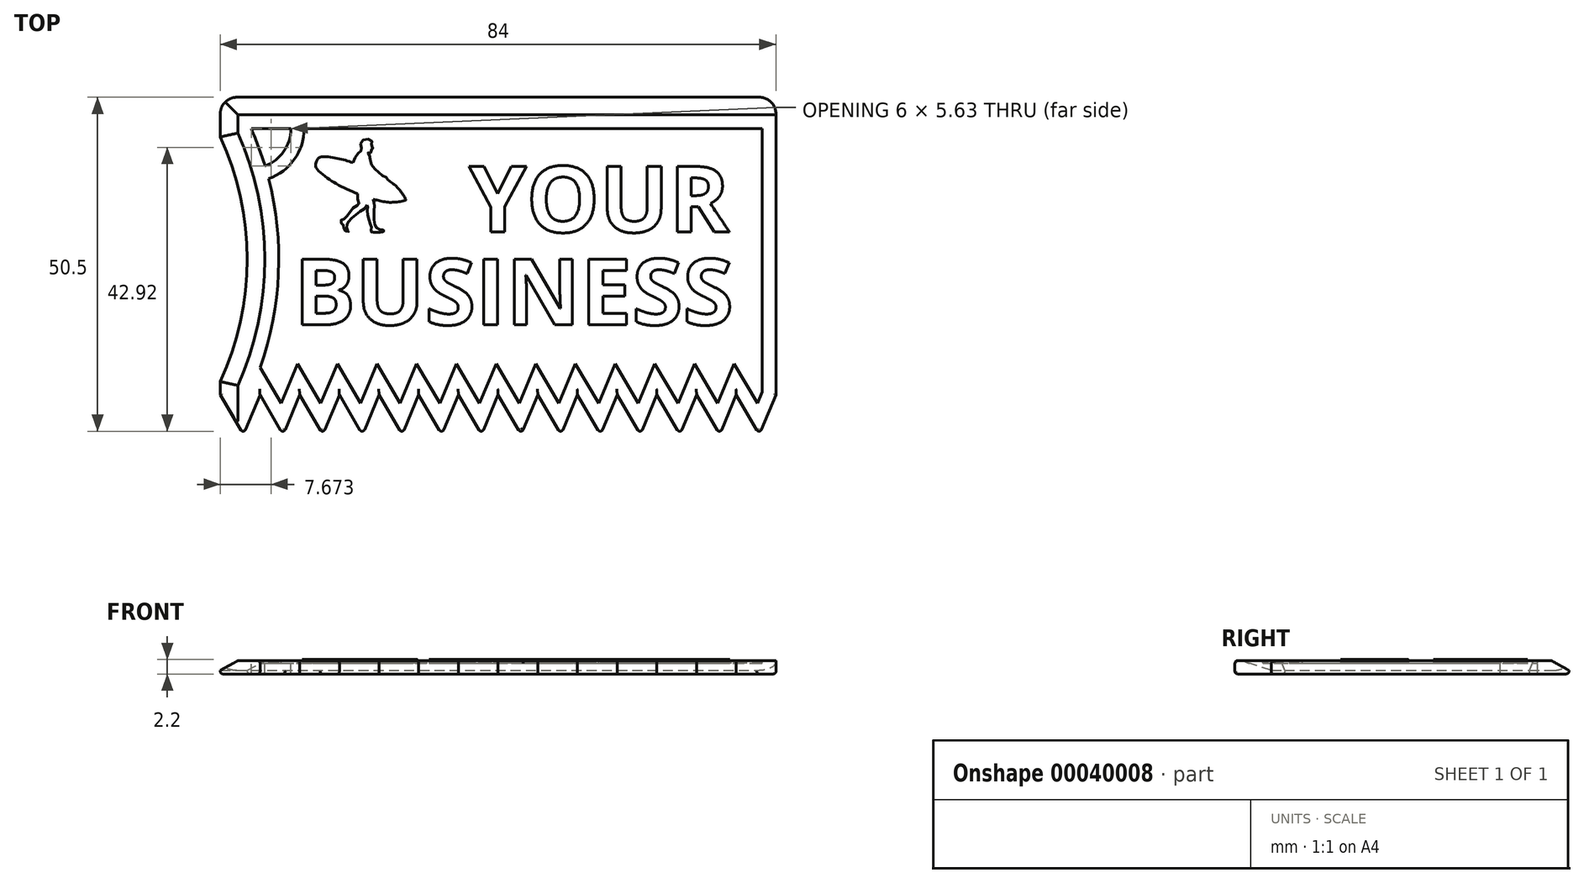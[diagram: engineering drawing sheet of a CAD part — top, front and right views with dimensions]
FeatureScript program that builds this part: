
annotation { "Feature Type Name" : "Feature", "Feature Type Description" : "" }
export const myFeature = defineFeature(function(context is Context, id is Id, definition is map)
    precondition{}
    {
        {
            assignVariable(context, id + "F0", {"name" : "t", "anyValue" : 2});
        }
        {
            var Q0;
            Q0=qCreatedBy(makeId("Top.planeOp"),FACE);
            var sketch = newSketch(context, id + "F1", { "sketchPlane" : qUnion([Q0])});
            skLineSegment(sketch, "E0.bottom", {"start": v(84, 51) * mm, "end": v(0, 51) * mm});
            skLineSegment(sketch, "E0.top", {"start": v(81.5, 0) * mm, "end": v(3.5, 0) * mm, "construction": true});
            skLineSegment(sketch, "E0.left", {"start": v(84, 51) * mm, "end": v(84, 6) * mm});
            skLineSegment(sketch, "E0.right", {"start": v(0, 51) * mm, "end": v(0, 6) * mm, "construction": true});
            skLineSegment(sketch, "E1", {"start": v(84, 6) * mm, "end": v(0, 6) * mm, "construction": true});
            skLineSegment(sketch, "E2", {"start": v(84, 6) * mm, "end": v(81.5, 0) * mm});
            skLineSegment(sketch, "E3", {"start": v(81.5, 0) * mm, "end": v(78, 6) * mm});
            skLineSegment(sketch, "E4.1.0.0", {"start": v(78, 6) * mm, "end": v(75.5, 0) * mm});
            skLineSegment(sketch, "E4.1.0.1", {"start": v(75.5, 0) * mm, "end": v(72, 6) * mm});
            skLineSegment(sketch, "E4.2.0.0", {"start": v(72, 6) * mm, "end": v(69.5, 0) * mm});
            skLineSegment(sketch, "E4.2.0.1", {"start": v(69.5, 0) * mm, "end": v(66, 6) * mm});
            skLineSegment(sketch, "E4.3.0.0", {"start": v(66, 6) * mm, "end": v(63.5, 0) * mm});
            skLineSegment(sketch, "E4.3.0.1", {"start": v(63.5, 0) * mm, "end": v(60, 6) * mm});
            skLineSegment(sketch, "E4.4.0.0", {"start": v(60, 6) * mm, "end": v(57.5, 0) * mm});
            skLineSegment(sketch, "E4.4.0.1", {"start": v(57.5, 0) * mm, "end": v(54, 6) * mm});
            skLineSegment(sketch, "E4.5.0.0", {"start": v(54, 6) * mm, "end": v(51.5, 0) * mm});
            skLineSegment(sketch, "E4.5.0.1", {"start": v(51.5, 0) * mm, "end": v(48, 6) * mm});
            skLineSegment(sketch, "E4.6.0.0", {"start": v(48, 6) * mm, "end": v(45.5, 0) * mm});
            skLineSegment(sketch, "E4.6.0.1", {"start": v(45.5, 0) * mm, "end": v(42, 6) * mm});
            skLineSegment(sketch, "E4.7.0.0", {"start": v(42, 6) * mm, "end": v(39.5, 0) * mm});
            skLineSegment(sketch, "E4.7.0.1", {"start": v(39.5, 0) * mm, "end": v(36, 6) * mm});
            skLineSegment(sketch, "E4.8.0.0", {"start": v(36, 6) * mm, "end": v(33.5, 0) * mm});
            skLineSegment(sketch, "E4.8.0.1", {"start": v(33.5, 0) * mm, "end": v(30, 6) * mm});
            skLineSegment(sketch, "E4.9.0.0", {"start": v(30, 6) * mm, "end": v(27.5, 0) * mm});
            skLineSegment(sketch, "E4.9.0.1", {"start": v(27.5, 0) * mm, "end": v(24, 6) * mm});
            skLineSegment(sketch, "E4.10.0.0", {"start": v(24, 6) * mm, "end": v(21.5, 0) * mm});
            skLineSegment(sketch, "E4.10.0.1", {"start": v(21.5, 0) * mm, "end": v(18, 6) * mm});
            skLineSegment(sketch, "E4.11.0.0", {"start": v(18, 6) * mm, "end": v(15.5, 0) * mm});
            skLineSegment(sketch, "E4.11.0.1", {"start": v(15.5, 0) * mm, "end": v(12, 6) * mm});
            skLineSegment(sketch, "E4.12.0.0", {"start": v(12, 6) * mm, "end": v(9.5, 0) * mm});
            skLineSegment(sketch, "E4.12.0.1", {"start": v(9.5, 0) * mm, "end": v(6, 6) * mm});
            skLineSegment(sketch, "E4.13.0.0", {"start": v(6, 6) * mm, "end": v(3.5, 0) * mm});
            skLineSegment(sketch, "E4.13.0.1", {"start": v(3.5, 0) * mm, "end": v(0, 6) * mm});
            skLineSegment(sketch, "E4.direction1", {"start": v(84, 6) * mm, "end": v(78, 6) * mm, "construction": true});
            skLineSegment(sketch, "E5", {"start": v(0, 6) * mm, "end": v(0, 8) * mm});
            skArc(sketch, "E6", {"start": v(0, 8) * mm, "mid": v(4.07, 26.5) * mm, "end": v(0, 45) * mm});
            skLineSegment(sketch, "E7", {"start": v(0, 45) * mm, "end": v(0, 51) * mm});
            skLineSegment(sketch, "E8", {"start": v(0, 6) * mm, "end": v(0, 0) * mm, "construction": true});
            skSolve(sketch);
        }
        {
            var Q0;
            Q0=qSketchRegion(id+"F1",true);
            extrude(context, id + "F2", {"entities" : qUnion([Q0]), "depth" : (getVariable(context, 't')) * mm});
        }
        {
            var Q0;
            Q0=makeQuery(id+"F2.opExtrude","CAP_EDGE",EDGE,{"disambiguationData":[OSD([sQuery(id+"F1.wireOp",EDGE,"E5")])],"isStart":false});
            var Q1;
            Q1=makeQuery(id+"F2.opExtrude","CAP_EDGE",EDGE,{"disambiguationData":[OSD([sQuery(id+"F1.wireOp",EDGE,"E6")])],"isStart":false});
            var Q2;
            Q2=makeQuery(id+"F2.opExtrude","CAP_EDGE",EDGE,{"disambiguationData":[OSD([sQuery(id+"F1.wireOp",EDGE,"E0.bottom")])],"isStart":false});
            var Q3;
            Q3=makeQuery(id+"F2.opExtrude","CAP_EDGE",EDGE,{"disambiguationData":[OSD([sQuery(id+"F1.wireOp",EDGE,"E7")])],"isStart":false});
            chamfer(context, id + "F3", {"entities" : qUnion([Q0, Q1, Q2, Q3]), "chamferType" : ChamferType.TWO_OFFSETS, "width1" : (getVariable(context, 't') * 2.2 / 3) * mm, "oppositeDirection" : false, "width2" : (getVariable(context, 't') * 4 / 3) * mm, "tangentPropagation" : true});
        }
        {
            var Q0;
            Q0=makeQuery(id+"F2.opExtrude","SWEPT_EDGE",EDGE,{"disambiguationData":[OSD([sQuery(id+"F1.wireOp",EDGE,"E0.bottom"),sQuery(id+"F1.wireOp",EDGE,"E7")])]});
            var Q1;
            Q1=makeQuery(id+"F2.opExtrude","SWEPT_EDGE",EDGE,{"disambiguationData":[OSD([sQuery(id+"F1.wireOp",EDGE,"E0.bottom"),sQuery(id+"F1.wireOp",EDGE,"E0.left")])]});
            fillet(context, id + "F4", {"entities" : qUnion([Q0, Q1]), "radius" : 2.5 * mm, "tangentPropagation" : true, "allowEdgeOverflow" : false});
        }
        {
            var Q0;
            Q0=makeQuery(id+"F2.opExtrude","CAP_FACE",FACE,{"disambiguationData":[OSD([sQuery(id+"F1.wireOp",EDGE,"E0.bottom"),sQuery(id+"F1.wireOp",EDGE,"E0.left"),sQuery(id+"F1.wireOp",EDGE,"E2"),sQuery(id+"F1.wireOp",EDGE,"E3"),sQuery(id+"F1.wireOp",EDGE,"E4.1.0.0"),sQuery(id+"F1.wireOp",EDGE,"E4.1.0.1"),sQuery(id+"F1.wireOp",EDGE,"E4.2.0.0"),sQuery(id+"F1.wireOp",EDGE,"E4.2.0.1"),sQuery(id+"F1.wireOp",EDGE,"E4.3.0.0"),sQuery(id+"F1.wireOp",EDGE,"E4.3.0.1"),sQuery(id+"F1.wireOp",EDGE,"E4.4.0.0"),sQuery(id+"F1.wireOp",EDGE,"E4.4.0.1"),sQuery(id+"F1.wireOp",EDGE,"E4.5.0.0"),sQuery(id+"F1.wireOp",EDGE,"E4.5.0.1"),sQuery(id+"F1.wireOp",EDGE,"E4.6.0.0"),sQuery(id+"F1.wireOp",EDGE,"E4.6.0.1"),sQuery(id+"F1.wireOp",EDGE,"E4.7.0.0"),sQuery(id+"F1.wireOp",EDGE,"E4.7.0.1"),sQuery(id+"F1.wireOp",EDGE,"E4.8.0.0"),sQuery(id+"F1.wireOp",EDGE,"E4.8.0.1"),sQuery(id+"F1.wireOp",EDGE,"E4.9.0.0"),sQuery(id+"F1.wireOp",EDGE,"E4.9.0.1"),sQuery(id+"F1.wireOp",EDGE,"E4.10.0.0"),sQuery(id+"F1.wireOp",EDGE,"E4.10.0.1"),sQuery(id+"F1.wireOp",EDGE,"E4.11.0.0"),sQuery(id+"F1.wireOp",EDGE,"E4.11.0.1"),sQuery(id+"F1.wireOp",EDGE,"E4.12.0.0"),sQuery(id+"F1.wireOp",EDGE,"E4.12.0.1"),sQuery(id+"F1.wireOp",EDGE,"E4.13.0.0"),sQuery(id+"F1.wireOp",EDGE,"E4.13.0.1"),sQuery(id+"F1.wireOp",EDGE,"E5"),sQuery(id+"F1.wireOp",EDGE,"E6"),sQuery(id+"F1.wireOp",EDGE,"E7")])],"isStart":false});
            var sketch = newSketch(context, id + "F5", { "sketchPlane" : qUnion([Q0])});
            skLineSegment(sketch, "E9.0", {"start": v(81.9, 6.42) * mm, "end": v(81.9, 46.23) * mm});
            skLineSegment(sketch, "E9.1", {"start": v(81.19, 4.7) * mm, "end": v(81.9, 6.42) * mm});
            skLineSegment(sketch, "E9.2", {"start": v(77.69, 10.7) * mm, "end": v(81.19, 4.7) * mm});
            skLineSegment(sketch, "E9.3", {"start": v(75.19, 4.7) * mm, "end": v(77.69, 10.7) * mm});
            skLineSegment(sketch, "E9.4", {"start": v(71.69, 10.7) * mm, "end": v(75.19, 4.7) * mm});
            skLineSegment(sketch, "E9.5", {"start": v(69.19, 4.7) * mm, "end": v(71.69, 10.7) * mm});
            skLineSegment(sketch, "E9.6", {"start": v(65.69, 10.7) * mm, "end": v(69.19, 4.7) * mm});
            skLineSegment(sketch, "E9.7", {"start": v(81.9, 46.23) * mm, "end": v(4.67, 46.23) * mm});
            skArc(sketch, "E9.8", {"start": v(4.67, 46.23) * mm, "mid": v(8.8, 28.32) * mm, "end": v(6.02, 10.14) * mm});
            skLineSegment(sketch, "E9.9", {"start": v(6.02, 10.14) * mm, "end": v(9.19, 4.7) * mm});
            skLineSegment(sketch, "E9.10", {"start": v(9.19, 4.7) * mm, "end": v(11.69, 10.7) * mm});
            skLineSegment(sketch, "E9.11", {"start": v(11.69, 10.7) * mm, "end": v(15.19, 4.7) * mm});
            skLineSegment(sketch, "E9.12", {"start": v(15.19, 4.7) * mm, "end": v(17.69, 10.7) * mm});
            skLineSegment(sketch, "E9.13", {"start": v(17.69, 10.7) * mm, "end": v(21.19, 4.7) * mm});
            skLineSegment(sketch, "E9.14", {"start": v(21.19, 4.7) * mm, "end": v(23.69, 10.7) * mm});
            skLineSegment(sketch, "E9.15", {"start": v(23.69, 10.7) * mm, "end": v(27.19, 4.7) * mm});
            skLineSegment(sketch, "E9.16", {"start": v(27.19, 4.7) * mm, "end": v(29.69, 10.7) * mm});
            skLineSegment(sketch, "E9.17", {"start": v(29.69, 10.7) * mm, "end": v(33.19, 4.7) * mm});
            skLineSegment(sketch, "E9.18", {"start": v(33.19, 4.7) * mm, "end": v(35.69, 10.7) * mm});
            skLineSegment(sketch, "E9.19", {"start": v(35.69, 10.7) * mm, "end": v(39.19, 4.7) * mm});
            skLineSegment(sketch, "E9.20", {"start": v(39.19, 4.7) * mm, "end": v(41.69, 10.7) * mm});
            skLineSegment(sketch, "E9.21", {"start": v(41.69, 10.7) * mm, "end": v(45.19, 4.7) * mm});
            skLineSegment(sketch, "E9.22", {"start": v(45.19, 4.7) * mm, "end": v(47.69, 10.7) * mm});
            skLineSegment(sketch, "E9.23", {"start": v(47.69, 10.7) * mm, "end": v(51.19, 4.7) * mm});
            skLineSegment(sketch, "E9.24", {"start": v(51.19, 4.7) * mm, "end": v(53.69, 10.7) * mm});
            skLineSegment(sketch, "E9.25", {"start": v(53.69, 10.7) * mm, "end": v(57.19, 4.7) * mm});
            skLineSegment(sketch, "E9.26", {"start": v(57.19, 4.7) * mm, "end": v(59.69, 10.7) * mm});
            skLineSegment(sketch, "E9.27", {"start": v(59.69, 10.7) * mm, "end": v(63.19, 4.7) * mm});
            skLineSegment(sketch, "E9.28", {"start": v(63.19, 4.7) * mm, "end": v(65.69, 10.7) * mm});
            skSolve(sketch);
        }
        {
            var Q0;
            Q0=makeQuery(id+"F5.imprint","IMPRINT",FACE,{"disambiguationData":[TD([[makeQuery(id+"F5.imprint","IMPRINT",EDGE,{"derivedFrom":sQuery(id+"F5.wireOp",EDGE,"E9.0")}),1.0]])]});
            extrude(context, id + "F6", {"entities" : qUnion([Q0]), "operationType" : NewBodyOperationType.REMOVE, "oppositeDirection" : true, "depth" : (getVariable(context, 't') / 5) * mm});
        }
        {
            var Q0;
            Q0=makeQuery(id+"F2.opExtrude","CAP_FACE",FACE,{"disambiguationData":[OSD([sQuery(id+"F1.wireOp",EDGE,"E0.bottom"),sQuery(id+"F1.wireOp",EDGE,"E0.left"),sQuery(id+"F1.wireOp",EDGE,"E2"),sQuery(id+"F1.wireOp",EDGE,"E3"),sQuery(id+"F1.wireOp",EDGE,"E4.1.0.0"),sQuery(id+"F1.wireOp",EDGE,"E4.1.0.1"),sQuery(id+"F1.wireOp",EDGE,"E4.2.0.0"),sQuery(id+"F1.wireOp",EDGE,"E4.2.0.1"),sQuery(id+"F1.wireOp",EDGE,"E4.3.0.0"),sQuery(id+"F1.wireOp",EDGE,"E4.3.0.1"),sQuery(id+"F1.wireOp",EDGE,"E4.4.0.0"),sQuery(id+"F1.wireOp",EDGE,"E4.4.0.1"),sQuery(id+"F1.wireOp",EDGE,"E4.5.0.0"),sQuery(id+"F1.wireOp",EDGE,"E4.5.0.1"),sQuery(id+"F1.wireOp",EDGE,"E4.6.0.0"),sQuery(id+"F1.wireOp",EDGE,"E4.6.0.1"),sQuery(id+"F1.wireOp",EDGE,"E4.7.0.0"),sQuery(id+"F1.wireOp",EDGE,"E4.7.0.1"),sQuery(id+"F1.wireOp",EDGE,"E4.8.0.0"),sQuery(id+"F1.wireOp",EDGE,"E4.8.0.1"),sQuery(id+"F1.wireOp",EDGE,"E4.9.0.0"),sQuery(id+"F1.wireOp",EDGE,"E4.9.0.1"),sQuery(id+"F1.wireOp",EDGE,"E4.10.0.0"),sQuery(id+"F1.wireOp",EDGE,"E4.10.0.1"),sQuery(id+"F1.wireOp",EDGE,"E4.11.0.0"),sQuery(id+"F1.wireOp",EDGE,"E4.11.0.1"),sQuery(id+"F1.wireOp",EDGE,"E4.12.0.0"),sQuery(id+"F1.wireOp",EDGE,"E4.12.0.1"),sQuery(id+"F1.wireOp",EDGE,"E4.13.0.0"),sQuery(id+"F1.wireOp",EDGE,"E4.13.0.1"),sQuery(id+"F1.wireOp",EDGE,"E5"),sQuery(id+"F1.wireOp",EDGE,"E6"),sQuery(id+"F1.wireOp",EDGE,"E7")])],"isStart":true});
            var Q1;
            Q1=makeQuery(id+"F2.opExtrude","CAP_EDGE",EDGE,{"disambiguationData":[OSD([sQuery(id+"F1.wireOp",EDGE,"E4.13.0.1")])],"isStart":false});
            var Q2;
            Q2=makeQuery(id+"F2.opExtrude","CAP_EDGE",EDGE,{"disambiguationData":[OSD([sQuery(id+"F1.wireOp",EDGE,"E4.13.0.0")])],"isStart":false});
            var Q3;
            Q3=makeQuery(id+"F2.opExtrude","SWEPT_EDGE",EDGE,{"disambiguationData":[OSD([sQuery(id+"F1.wireOp",EDGE,"E4.13.0.0"),sQuery(id+"F1.wireOp",EDGE,"E4.13.0.1")])]});
            var Q4;
            Q4=makeQuery(id+"F2.opExtrude","CAP_EDGE",EDGE,{"disambiguationData":[OSD([sQuery(id+"F1.wireOp",EDGE,"E4.12.0.1")])],"isStart":false});
            var Q5;
            Q5=makeQuery(id+"F2.opExtrude","SWEPT_EDGE",EDGE,{"disambiguationData":[OSD([sQuery(id+"F1.wireOp",EDGE,"E4.12.0.0"),sQuery(id+"F1.wireOp",EDGE,"E4.12.0.1")])]});
            var Q6;
            Q6=makeQuery(id+"F2.opExtrude","CAP_EDGE",EDGE,{"disambiguationData":[OSD([sQuery(id+"F1.wireOp",EDGE,"E4.12.0.0")])],"isStart":false});
            var Q7;
            Q7=makeQuery(id+"F2.opExtrude","CAP_EDGE",EDGE,{"disambiguationData":[OSD([sQuery(id+"F1.wireOp",EDGE,"E4.11.0.1")])],"isStart":false});
            var Q8;
            Q8=makeQuery(id+"F2.opExtrude","SWEPT_EDGE",EDGE,{"disambiguationData":[OSD([sQuery(id+"F1.wireOp",EDGE,"E4.11.0.0"),sQuery(id+"F1.wireOp",EDGE,"E4.11.0.1")])]});
            var Q9;
            Q9=makeQuery(id+"F2.opExtrude","CAP_EDGE",EDGE,{"disambiguationData":[OSD([sQuery(id+"F1.wireOp",EDGE,"E4.11.0.0")])],"isStart":false});
            var Q10;
            Q10=makeQuery(id+"F2.opExtrude","CAP_EDGE",EDGE,{"disambiguationData":[OSD([sQuery(id+"F1.wireOp",EDGE,"E4.10.0.1")])],"isStart":false});
            var Q11;
            Q11=makeQuery(id+"F2.opExtrude","CAP_EDGE",EDGE,{"disambiguationData":[OSD([sQuery(id+"F1.wireOp",EDGE,"E4.10.0.0")])],"isStart":false});
            var Q12;
            Q12=makeQuery(id+"F2.opExtrude","CAP_EDGE",EDGE,{"disambiguationData":[OSD([sQuery(id+"F1.wireOp",EDGE,"E4.9.0.1")])],"isStart":false});
            var Q13;
            Q13=makeQuery(id+"F2.opExtrude","CAP_EDGE",EDGE,{"disambiguationData":[OSD([sQuery(id+"F1.wireOp",EDGE,"E4.9.0.0")])],"isStart":false});
            var Q14;
            Q14=makeQuery(id+"F2.opExtrude","CAP_EDGE",EDGE,{"disambiguationData":[OSD([sQuery(id+"F1.wireOp",EDGE,"E4.8.0.1")])],"isStart":false});
            var Q15;
            Q15=makeQuery(id+"F2.opExtrude","CAP_EDGE",EDGE,{"disambiguationData":[OSD([sQuery(id+"F1.wireOp",EDGE,"E4.8.0.0")])],"isStart":false});
            var Q16;
            Q16=makeQuery(id+"F2.opExtrude","CAP_EDGE",EDGE,{"disambiguationData":[OSD([sQuery(id+"F1.wireOp",EDGE,"E4.7.0.1")])],"isStart":false});
            var Q17;
            Q17=makeQuery(id+"F2.opExtrude","CAP_EDGE",EDGE,{"disambiguationData":[OSD([sQuery(id+"F1.wireOp",EDGE,"E4.7.0.0")])],"isStart":false});
            var Q18;
            Q18=makeQuery(id+"F2.opExtrude","CAP_EDGE",EDGE,{"disambiguationData":[OSD([sQuery(id+"F1.wireOp",EDGE,"E4.6.0.1")])],"isStart":false});
            var Q19;
            Q19=makeQuery(id+"F2.opExtrude","CAP_EDGE",EDGE,{"disambiguationData":[OSD([sQuery(id+"F1.wireOp",EDGE,"E4.6.0.0")])],"isStart":false});
            var Q20;
            Q20=makeQuery(id+"F2.opExtrude","CAP_EDGE",EDGE,{"disambiguationData":[OSD([sQuery(id+"F1.wireOp",EDGE,"E4.5.0.1")])],"isStart":false});
            var Q21;
            Q21=makeQuery(id+"F2.opExtrude","CAP_EDGE",EDGE,{"disambiguationData":[OSD([sQuery(id+"F1.wireOp",EDGE,"E4.5.0.0")])],"isStart":false});
            var Q22;
            Q22=makeQuery(id+"F2.opExtrude","CAP_EDGE",EDGE,{"disambiguationData":[OSD([sQuery(id+"F1.wireOp",EDGE,"E4.4.0.1")])],"isStart":false});
            var Q23;
            Q23=makeQuery(id+"F2.opExtrude","CAP_EDGE",EDGE,{"disambiguationData":[OSD([sQuery(id+"F1.wireOp",EDGE,"E4.4.0.0")])],"isStart":false});
            var Q24;
            Q24=makeQuery(id+"F2.opExtrude","CAP_EDGE",EDGE,{"disambiguationData":[OSD([sQuery(id+"F1.wireOp",EDGE,"E4.3.0.1")])],"isStart":false});
            var Q25;
            Q25=makeQuery(id+"F2.opExtrude","CAP_EDGE",EDGE,{"disambiguationData":[OSD([sQuery(id+"F1.wireOp",EDGE,"E4.3.0.0")])],"isStart":false});
            var Q26;
            Q26=makeQuery(id+"F2.opExtrude","CAP_EDGE",EDGE,{"disambiguationData":[OSD([sQuery(id+"F1.wireOp",EDGE,"E4.2.0.1")])],"isStart":false});
            var Q27;
            Q27=makeQuery(id+"F2.opExtrude","CAP_EDGE",EDGE,{"disambiguationData":[OSD([sQuery(id+"F1.wireOp",EDGE,"E4.2.0.0")])],"isStart":false});
            var Q28;
            Q28=makeQuery(id+"F2.opExtrude","CAP_EDGE",EDGE,{"disambiguationData":[OSD([sQuery(id+"F1.wireOp",EDGE,"E4.1.0.1")])],"isStart":false});
            var Q29;
            Q29=makeQuery(id+"F2.opExtrude","CAP_EDGE",EDGE,{"disambiguationData":[OSD([sQuery(id+"F1.wireOp",EDGE,"E4.1.0.0")])],"isStart":false});
            var Q30;
            Q30=makeQuery(id+"F2.opExtrude","CAP_EDGE",EDGE,{"disambiguationData":[OSD([sQuery(id+"F1.wireOp",EDGE,"E3")])],"isStart":false});
            var Q31;
            Q31=makeQuery(id+"F2.opExtrude","SWEPT_EDGE",EDGE,{"disambiguationData":[OSD([sQuery(id+"F1.wireOp",EDGE,"E2"),sQuery(id+"F1.wireOp",EDGE,"E3")])]});
            var Q32;
            Q32=makeQuery(id+"F2.opExtrude","CAP_EDGE",EDGE,{"disambiguationData":[OSD([sQuery(id+"F1.wireOp",EDGE,"E2")])],"isStart":false});
            var Q33;
            Q33=makeQuery(id+"F2.opExtrude","SWEPT_EDGE",EDGE,{"disambiguationData":[OSD([sQuery(id+"F1.wireOp",EDGE,"E4.1.0.0"),sQuery(id+"F1.wireOp",EDGE,"E4.1.0.1")])]});
            var Q34;
            Q34=makeQuery(id+"F2.opExtrude","SWEPT_EDGE",EDGE,{"disambiguationData":[OSD([sQuery(id+"F1.wireOp",EDGE,"E4.2.0.0"),sQuery(id+"F1.wireOp",EDGE,"E4.2.0.1")])]});
            var Q35;
            Q35=makeQuery(id+"F2.opExtrude","SWEPT_EDGE",EDGE,{"disambiguationData":[OSD([sQuery(id+"F1.wireOp",EDGE,"E4.3.0.0"),sQuery(id+"F1.wireOp",EDGE,"E4.3.0.1")])]});
            var Q36;
            Q36=makeQuery(id+"F2.opExtrude","SWEPT_EDGE",EDGE,{"disambiguationData":[OSD([sQuery(id+"F1.wireOp",EDGE,"E4.4.0.0"),sQuery(id+"F1.wireOp",EDGE,"E4.4.0.1")])]});
            var Q37;
            Q37=makeQuery(id+"F2.opExtrude","SWEPT_EDGE",EDGE,{"disambiguationData":[OSD([sQuery(id+"F1.wireOp",EDGE,"E4.5.0.0"),sQuery(id+"F1.wireOp",EDGE,"E4.5.0.1")])]});
            var Q38;
            Q38=makeQuery(id+"F2.opExtrude","SWEPT_EDGE",EDGE,{"disambiguationData":[OSD([sQuery(id+"F1.wireOp",EDGE,"E4.6.0.0"),sQuery(id+"F1.wireOp",EDGE,"E4.6.0.1")])]});
            var Q39;
            Q39=makeQuery(id+"F2.opExtrude","SWEPT_EDGE",EDGE,{"disambiguationData":[OSD([sQuery(id+"F1.wireOp",EDGE,"E4.7.0.0"),sQuery(id+"F1.wireOp",EDGE,"E4.7.0.1")])]});
            var Q40;
            Q40=makeQuery(id+"F2.opExtrude","SWEPT_EDGE",EDGE,{"disambiguationData":[OSD([sQuery(id+"F1.wireOp",EDGE,"E4.8.0.0"),sQuery(id+"F1.wireOp",EDGE,"E4.8.0.1")])]});
            var Q41;
            Q41=makeQuery(id+"F2.opExtrude","SWEPT_EDGE",EDGE,{"disambiguationData":[OSD([sQuery(id+"F1.wireOp",EDGE,"E4.9.0.0"),sQuery(id+"F1.wireOp",EDGE,"E4.9.0.1")])]});
            var Q42;
            Q42=makeQuery(id+"F2.opExtrude","SWEPT_EDGE",EDGE,{"disambiguationData":[OSD([sQuery(id+"F1.wireOp",EDGE,"E4.10.0.0"),sQuery(id+"F1.wireOp",EDGE,"E4.10.0.1")])]});
            fillet(context, id + "F7", {"entities" : qUnion([Q0, Q1, Q2, Q3, Q4, Q5, Q6, Q7, Q8, Q9, Q10, Q11, Q12, Q13, Q14, Q15, Q16, Q17, Q18, Q19, Q20, Q21, Q22, Q23, Q24, Q25, Q26, Q27, Q28, Q29, Q30, Q31, Q32, Q33, Q34, Q35, Q36, Q37, Q38, Q39, Q40, Q41, Q42]), "radius" : .4 * mm, "tangentPropagation" : true, "allowEdgeOverflow" : false});
        }
        {
            var Q0;
            Q0=makeQuery(id+"F6.boolean.opBoolean","COPY",FACE,{"derivedFrom":makeQuery(id+"F6.opExtrude","CAP_FACE",FACE,{"disambiguationData":[OSD([sQuery(id+"F5.wireOp",EDGE,"E9.0"),sQuery(id+"F5.wireOp",EDGE,"E9.1"),sQuery(id+"F5.wireOp",EDGE,"E9.2"),sQuery(id+"F5.wireOp",EDGE,"E9.3"),sQuery(id+"F5.wireOp",EDGE,"E9.4"),sQuery(id+"F5.wireOp",EDGE,"E9.5"),sQuery(id+"F5.wireOp",EDGE,"E9.6"),sQuery(id+"F5.wireOp",EDGE,"E9.7"),sQuery(id+"F5.wireOp",EDGE,"E9.8"),sQuery(id+"F5.wireOp",EDGE,"E9.9"),sQuery(id+"F5.wireOp",EDGE,"E9.10"),sQuery(id+"F5.wireOp",EDGE,"E9.11"),sQuery(id+"F5.wireOp",EDGE,"E9.12"),sQuery(id+"F5.wireOp",EDGE,"E9.13"),sQuery(id+"F5.wireOp",EDGE,"E9.14"),sQuery(id+"F5.wireOp",EDGE,"E9.15"),sQuery(id+"F5.wireOp",EDGE,"E9.16"),sQuery(id+"F5.wireOp",EDGE,"E9.17"),sQuery(id+"F5.wireOp",EDGE,"E9.18"),sQuery(id+"F5.wireOp",EDGE,"E9.19"),sQuery(id+"F5.wireOp",EDGE,"E9.20"),sQuery(id+"F5.wireOp",EDGE,"E9.21"),sQuery(id+"F5.wireOp",EDGE,"E9.22"),sQuery(id+"F5.wireOp",EDGE,"E9.23"),sQuery(id+"F5.wireOp",EDGE,"E9.24"),sQuery(id+"F5.wireOp",EDGE,"E9.25"),sQuery(id+"F5.wireOp",EDGE,"E9.26"),sQuery(id+"F5.wireOp",EDGE,"E9.27"),sQuery(id+"F5.wireOp",EDGE,"E9.28")])],"isStart":false})});
            var sketch = newSketch(context, id + "F8", { "sketchPlane" : qUnion([Q0])});
            skText(sketch, "E10", { "text": "BUSINESS", "fontName": "OpenSans-Bold.ttf"});
            skText(sketch, "E11", { "text": "YOUR", "fontName": "OpenSans-Bold.ttf"});
            const initialGuessF8  = {"E10": [0.0111, 0.01661, 1, 0, 0.01], "E11": [0.0376, 0.03061, 1, 0, 0.01]};
            skSetInitialGuess(sketch, initialGuessF8);
            skSolve(sketch);
        }
        {
            var Q0;
            Q0=makeQuery(id+"F8.imprint","IMPRINT",FACE,{"disambiguationData":[TD([[makeQuery(id+"F8.imprint","IMPRINT",EDGE,{"derivedFrom":sQuery(id+"F8.wireOp",EDGE,"E10.sketch_text.stroke-0")}),1.0]])]});
            var sketch = newSketch(context, id + "F9", { "sketchPlane" : qUnion([Q0])});
            skLineSegment(sketch, "E12.0", {"start": v(81.9, 46.23) * mm, "end": v(4.67, 46.23) * mm});
            skArc(sketch, "E12.1", {"start": v(4.67, 46.23) * mm, "mid": v(8.8, 28.32) * mm, "end": v(6.02, 10.14) * mm});
            skPoint(sketch, "E12.2", {"position": v(4.67, 46.23) * mm});
            skArc(sketch, "E13", {"start": v(6.76, 40.6) * mm, "mid": v(9.6, 42.8) * mm, "end": v(10.67, 46.23) * mm});
            skArc(sketch, "E14", {"start": v(7.3, 38.68) * mm, "mid": v(11.2, 41.6) * mm, "end": v(12.67, 46.23) * mm});
            skLineSegment(sketch, "E15", {"start": v(14.33, 41.37) * mm, "end": v(28.35, 35.34) * mm, "construction": true});
            skFitSpline(sketch, "E16", {"points": [v(20.78, 36.4) * mm, v(18.17, 37.57) * mm, v(16.2, 38.77) * mm, v(14.57, 40.2) * mm, v(14.39, 40.75) * mm, v(14.51, 41.3) * mm], "startDerivative": vector(-8.18, 3.62) * mm, "endDerivative": vector(1.44, 4.42) * mm});
            skFitSpline(sketch, "E17", {"points": [v(21.8, 40.38) * mm, v(19.73, 41.2) * mm, v(17.5, 41.8) * mm, v(15.34, 42) * mm, v(14.82, 41.76) * mm, v(14.51, 41.3) * mm], "startDerivative": vector(-8.26, 3.44) * mm, "endDerivative": vector(-2.21, -4.08) * mm});
            skFitSpline(sketch, "E18", {"points": [v(20.78, 36.4) * mm, v(20.78, 35.64) * mm, v(20.95, 35.07) * mm, v(20.96, 34.8) * mm, v(20.8, 34.66) * mm, v(20.25, 34.4) * mm, v(19.79, 33.88) * mm, v(19.35, 33.26) * mm, v(19, 32.82) * mm, v(18.79, 32.65) * mm, v(18.48, 32.52) * mm, v(18.27, 32.44) * mm, v(18.2, 32.27) * mm, v(18.32, 31.93) * mm, v(18.48, 31.77) * mm, v(18.61, 31.65) * mm, v(18.65, 31.45) * mm, v(18.68, 31.05) * mm, v(18.84, 30.85) * mm, v(19.05, 30.74) * mm, v(19.33, 30.68) * mm, v(19.38, 30.7) * mm, v(19.39, 30.75) * mm, v(19.36, 30.83) * mm, v(19.24, 30.92) * mm, v(19.13, 31.03) * mm, v(19.11, 31.31) * mm, v(19.14, 31.62) * mm, v(19.17, 31.85) * mm, v(19.25, 32.01) * mm, v(19.45, 32.31) * mm, v(19.98, 32.83) * mm, v(20.57, 33.32) * mm, v(21.18, 33.76) * mm, v(21.73, 34.08) * mm, v(21.96, 34.28) * mm, v(22.05, 34.5) * mm, v(22.1, 34.7) * mm, v(22.15, 34.73) * mm, v(22.18, 34.73) * mm], "startDerivative": vector(-1.7, -19.21) * mm, "endDerivative": vector(3.01, -1.59) * mm});
            skFitSpline(sketch, "E19", {"points": [v(20.05, 41.08) * mm, v(20.31, 41.73) * mm, v(20.57, 42.25) * mm, v(20.85, 42.54) * mm, v(21.15, 42.79) * mm, v(21.36, 42.97) * mm, v(21.42, 43.1) * mm, v(21.3, 43.35) * mm, v(21.2, 43.69) * mm, v(21.26, 44.09) * mm, v(21.42, 44.41) * mm, v(21.96, 44.72) * mm, v(22.41, 44.65) * mm, v(22.73, 44.52) * mm, v(22.95, 44.3) * mm, v(22.93, 44.07) * mm, v(22.87, 43.95) * mm, v(22.93, 43.83) * mm, v(22.96, 43.68) * mm, v(22.91, 43.6) * mm, v(22.9, 43.54) * mm, v(22.98, 43.43) * mm, v(23.06, 43.31) * mm, v(23.06, 43.23) * mm, v(23.02, 43.17) * mm, v(22.9, 43.2) * mm, v(22.89, 43.13) * mm, v(22.89, 43.03) * mm, v(22.86, 42.96) * mm, v(22.81, 42.9) * mm, v(22.82, 42.8) * mm, v(22.85, 42.72) * mm, v(22.83, 42.65) * mm, v(22.74, 42.62) * mm, v(22.65, 42.58) * mm, v(22.47, 42.6) * mm, v(22.37, 42.6) * mm, v(22.3, 42.56) * mm, v(22.37, 42.46) * mm, v(22.53, 42.3) * mm, v(22.67, 41.97) * mm, v(22.68, 41.44) * mm, v(22.8, 40.96) * mm, v(23.02, 40.5) * mm, v(23.5, 40.04) * mm, v(23.89, 39.68) * mm, v(24.31, 39.38) * mm, v(24.62, 39.05) * mm, v(24.88, 38.93) * mm, v(25.2, 38.8) * mm, v(25.31, 38.6) * mm, v(25.34, 38.5) * mm], "startDerivative": vector(7.84, 19.36) * mm, "endDerivative": vector(2.4, -8.81) * mm});
            skFitSpline(sketch, "E20", {"points": [v(23.11, 35.6) * mm, v(23.77, 35.42) * mm, v(24.73, 35.21) * mm, v(25.68, 35.1) * mm, v(26.5, 35.15) * mm, v(27.4, 35.27) * mm, v(28.03, 35.44) * mm, v(28.05, 35.47) * mm], "startDerivative": vector(4.26, -1.27) * mm, "endDerivative": vector(0.24, 0.98) * mm});
            skFitSpline(sketch, "E21.MirrorCS", {"points": [v(24.56, 38.97) * mm, v(25.15, 38.62) * mm, v(25.96, 38.06) * mm, v(26.68, 37.45) * mm, v(27.23, 36.82) * mm, v(27.75, 36.09) * mm, v(28.06, 35.52) * mm, v(28.05, 35.47) * mm], "startDerivative": vector(3.85, -2.22) * mm, "endDerivative": vector(-0.55, -0.85) * mm});
            skFitSpline(sketch, "E22", {"points": [v(23.11, 35.6) * mm, v(23.22, 35.14) * mm, v(23.28, 34.82) * mm, v(23.26, 34.39) * mm, v(23.22, 33.76) * mm, v(23.23, 33.07) * mm, v(23.28, 32.27) * mm, v(23.41, 31.6) * mm, v(23.57, 31.3) * mm, v(23.85, 31.1) * mm, v(24.16, 31.01) * mm, v(24.42, 30.98) * mm, v(24.63, 30.93) * mm, v(24.73, 30.83) * mm, v(24.73, 30.75) * mm, v(24.68, 30.67) * mm, v(24.57, 30.62) * mm, v(24.4, 30.58) * mm, v(24.1, 30.57) * mm, v(23.65, 30.57) * mm, v(23.34, 30.59) * mm, v(23.1, 30.58) * mm, v(22.93, 30.59) * mm, v(22.84, 30.63) * mm, v(22.8, 30.76) * mm, v(22.8, 30.93) * mm, v(22.87, 31.1) * mm, v(22.87, 31.29) * mm, v(22.75, 31.62) * mm, v(22.54, 32.2) * mm, v(22.35, 32.86) * mm, v(22.2, 33.51) * mm, v(22.26, 34.1) * mm, v(22.28, 34.5) * mm, v(22.26, 34.67) * mm, v(22.18, 34.73) * mm], "startDerivative": vector(2.94, -13.83) * mm, "endDerivative": vector(-5.6, 2.93) * mm});
            skSolve(sketch);
        }
        {
            var Q0;
            Q0=qSketchRegion(id+"F8",true);
            var Q1;
            Q1=makeQuery(id+"F2.opExtrude","CAP_FACE",FACE,{"disambiguationData":[OSD([sQuery(id+"F1.wireOp",EDGE,"E0.bottom"),sQuery(id+"F1.wireOp",EDGE,"E0.left"),sQuery(id+"F1.wireOp",EDGE,"E2"),sQuery(id+"F1.wireOp",EDGE,"E3"),sQuery(id+"F1.wireOp",EDGE,"E4.1.0.0"),sQuery(id+"F1.wireOp",EDGE,"E4.1.0.1"),sQuery(id+"F1.wireOp",EDGE,"E4.2.0.0"),sQuery(id+"F1.wireOp",EDGE,"E4.2.0.1"),sQuery(id+"F1.wireOp",EDGE,"E4.3.0.0"),sQuery(id+"F1.wireOp",EDGE,"E4.3.0.1"),sQuery(id+"F1.wireOp",EDGE,"E4.4.0.0"),sQuery(id+"F1.wireOp",EDGE,"E4.4.0.1"),sQuery(id+"F1.wireOp",EDGE,"E4.5.0.0"),sQuery(id+"F1.wireOp",EDGE,"E4.5.0.1"),sQuery(id+"F1.wireOp",EDGE,"E4.6.0.0"),sQuery(id+"F1.wireOp",EDGE,"E4.6.0.1"),sQuery(id+"F1.wireOp",EDGE,"E4.7.0.0"),sQuery(id+"F1.wireOp",EDGE,"E4.7.0.1"),sQuery(id+"F1.wireOp",EDGE,"E4.8.0.0"),sQuery(id+"F1.wireOp",EDGE,"E4.8.0.1"),sQuery(id+"F1.wireOp",EDGE,"E4.9.0.0"),sQuery(id+"F1.wireOp",EDGE,"E4.9.0.1"),sQuery(id+"F1.wireOp",EDGE,"E4.10.0.0"),sQuery(id+"F1.wireOp",EDGE,"E4.10.0.1"),sQuery(id+"F1.wireOp",EDGE,"E4.11.0.0"),sQuery(id+"F1.wireOp",EDGE,"E4.11.0.1"),sQuery(id+"F1.wireOp",EDGE,"E4.12.0.0"),sQuery(id+"F1.wireOp",EDGE,"E4.12.0.1"),sQuery(id+"F1.wireOp",EDGE,"E4.13.0.0"),sQuery(id+"F1.wireOp",EDGE,"E4.13.0.1"),sQuery(id+"F1.wireOp",EDGE,"E5"),sQuery(id+"F1.wireOp",EDGE,"E6"),sQuery(id+"F1.wireOp",EDGE,"E7")])],"isStart":false});
            extrude(context, id + "F10", {"entities" : qUnion([Q0]), "operationType" : NewBodyOperationType.ADD, "endBoundEntityFace" : qUnion([Q1]), "depth" : .6 * mm});
        }
        {
            var Q0;
            {var subQ3=sQuery(id+"F9.wireOp",EDGE,"E13");Q0=makeQuery(id+"F9.imprint","IMPRINT",FACE,{"disambiguationData":[TD([[makeQuery(id+"F9.imprint","IMPRINT",EDGE,{"derivedFrom":subQ3}),1.0]])]});}
            extrude(context, id + "F11", {"entities" : qUnion([Q0]), "operationType" : NewBodyOperationType.REMOVE, "oppositeDirection" : true, "depth" : 25 * mm});
        }
        {
            var Q0;
            {var subQ0=sQuery(id+"F9.wireOp",EDGE,"E13");Q0=makeQuery(id+"F9.imprint","IMPRINT",FACE,{"disambiguationData":[TD([[makeQuery(id+"F9.imprint","IMPRINT",EDGE,{"derivedFrom":subQ0}),-1.0]])]});}
            var Q1;
            Q1=makeQuery(id+"F2.opExtrude","CAP_FACE",FACE,{"disambiguationData":[OSD([sQuery(id+"F1.wireOp",EDGE,"E0.bottom"),sQuery(id+"F1.wireOp",EDGE,"E0.left"),sQuery(id+"F1.wireOp",EDGE,"E2"),sQuery(id+"F1.wireOp",EDGE,"E3"),sQuery(id+"F1.wireOp",EDGE,"E4.1.0.0"),sQuery(id+"F1.wireOp",EDGE,"E4.1.0.1"),sQuery(id+"F1.wireOp",EDGE,"E4.2.0.0"),sQuery(id+"F1.wireOp",EDGE,"E4.2.0.1"),sQuery(id+"F1.wireOp",EDGE,"E4.3.0.0"),sQuery(id+"F1.wireOp",EDGE,"E4.3.0.1"),sQuery(id+"F1.wireOp",EDGE,"E4.4.0.0"),sQuery(id+"F1.wireOp",EDGE,"E4.4.0.1"),sQuery(id+"F1.wireOp",EDGE,"E4.5.0.0"),sQuery(id+"F1.wireOp",EDGE,"E4.5.0.1"),sQuery(id+"F1.wireOp",EDGE,"E4.6.0.0"),sQuery(id+"F1.wireOp",EDGE,"E4.6.0.1"),sQuery(id+"F1.wireOp",EDGE,"E4.7.0.0"),sQuery(id+"F1.wireOp",EDGE,"E4.7.0.1"),sQuery(id+"F1.wireOp",EDGE,"E4.8.0.0"),sQuery(id+"F1.wireOp",EDGE,"E4.8.0.1"),sQuery(id+"F1.wireOp",EDGE,"E4.9.0.0"),sQuery(id+"F1.wireOp",EDGE,"E4.9.0.1"),sQuery(id+"F1.wireOp",EDGE,"E4.10.0.0"),sQuery(id+"F1.wireOp",EDGE,"E4.10.0.1"),sQuery(id+"F1.wireOp",EDGE,"E4.11.0.0"),sQuery(id+"F1.wireOp",EDGE,"E4.11.0.1"),sQuery(id+"F1.wireOp",EDGE,"E4.12.0.0"),sQuery(id+"F1.wireOp",EDGE,"E4.12.0.1"),sQuery(id+"F1.wireOp",EDGE,"E4.13.0.0"),sQuery(id+"F1.wireOp",EDGE,"E4.13.0.1"),sQuery(id+"F1.wireOp",EDGE,"E5"),sQuery(id+"F1.wireOp",EDGE,"E6"),sQuery(id+"F1.wireOp",EDGE,"E7")])],"isStart":false});
            extrude(context, id + "F12", {"entities" : qUnion([Q0]), "operationType" : NewBodyOperationType.ADD, "endBound" : BoundingType.UP_TO_SURFACE, "endBoundEntityFace" : qUnion([Q1]), "depth" : 25 * mm});
        }
        {
            var Q0;
            Q0=makeQuery(id+"F9.imprint","IMPRINT",FACE,{"disambiguationData":[TD([[makeQuery(id+"F9.imprint","IMPRINT",EDGE,{"derivedFrom":sQuery(id+"F9.wireOp",EDGE,"E16")}),-1.0]])]});
            var Q1;
            Q1=makeQuery(id+"F2.opExtrude","CAP_FACE",FACE,{"disambiguationData":[OSD([sQuery(id+"F1.wireOp",EDGE,"E0.bottom"),sQuery(id+"F1.wireOp",EDGE,"E0.left"),sQuery(id+"F1.wireOp",EDGE,"E2"),sQuery(id+"F1.wireOp",EDGE,"E3"),sQuery(id+"F1.wireOp",EDGE,"E4.1.0.0"),sQuery(id+"F1.wireOp",EDGE,"E4.1.0.1"),sQuery(id+"F1.wireOp",EDGE,"E4.2.0.0"),sQuery(id+"F1.wireOp",EDGE,"E4.2.0.1"),sQuery(id+"F1.wireOp",EDGE,"E4.3.0.0"),sQuery(id+"F1.wireOp",EDGE,"E4.3.0.1"),sQuery(id+"F1.wireOp",EDGE,"E4.4.0.0"),sQuery(id+"F1.wireOp",EDGE,"E4.4.0.1"),sQuery(id+"F1.wireOp",EDGE,"E4.5.0.0"),sQuery(id+"F1.wireOp",EDGE,"E4.5.0.1"),sQuery(id+"F1.wireOp",EDGE,"E4.6.0.0"),sQuery(id+"F1.wireOp",EDGE,"E4.6.0.1"),sQuery(id+"F1.wireOp",EDGE,"E4.7.0.0"),sQuery(id+"F1.wireOp",EDGE,"E4.7.0.1"),sQuery(id+"F1.wireOp",EDGE,"E4.8.0.0"),sQuery(id+"F1.wireOp",EDGE,"E4.8.0.1"),sQuery(id+"F1.wireOp",EDGE,"E4.9.0.0"),sQuery(id+"F1.wireOp",EDGE,"E4.9.0.1"),sQuery(id+"F1.wireOp",EDGE,"E4.10.0.0"),sQuery(id+"F1.wireOp",EDGE,"E4.10.0.1"),sQuery(id+"F1.wireOp",EDGE,"E4.11.0.0"),sQuery(id+"F1.wireOp",EDGE,"E4.11.0.1"),sQuery(id+"F1.wireOp",EDGE,"E4.12.0.0"),sQuery(id+"F1.wireOp",EDGE,"E4.12.0.1"),sQuery(id+"F1.wireOp",EDGE,"E4.13.0.0"),sQuery(id+"F1.wireOp",EDGE,"E4.13.0.1"),sQuery(id+"F1.wireOp",EDGE,"E5"),sQuery(id+"F1.wireOp",EDGE,"E6"),sQuery(id+"F1.wireOp",EDGE,"E7")])],"isStart":false});
            extrude(context, id + "F13", {"entities" : qUnion([Q0]), "operationType" : NewBodyOperationType.ADD, "endBoundEntityFace" : qUnion([Q1]), "depth" : .6 * mm});
        }
    });
